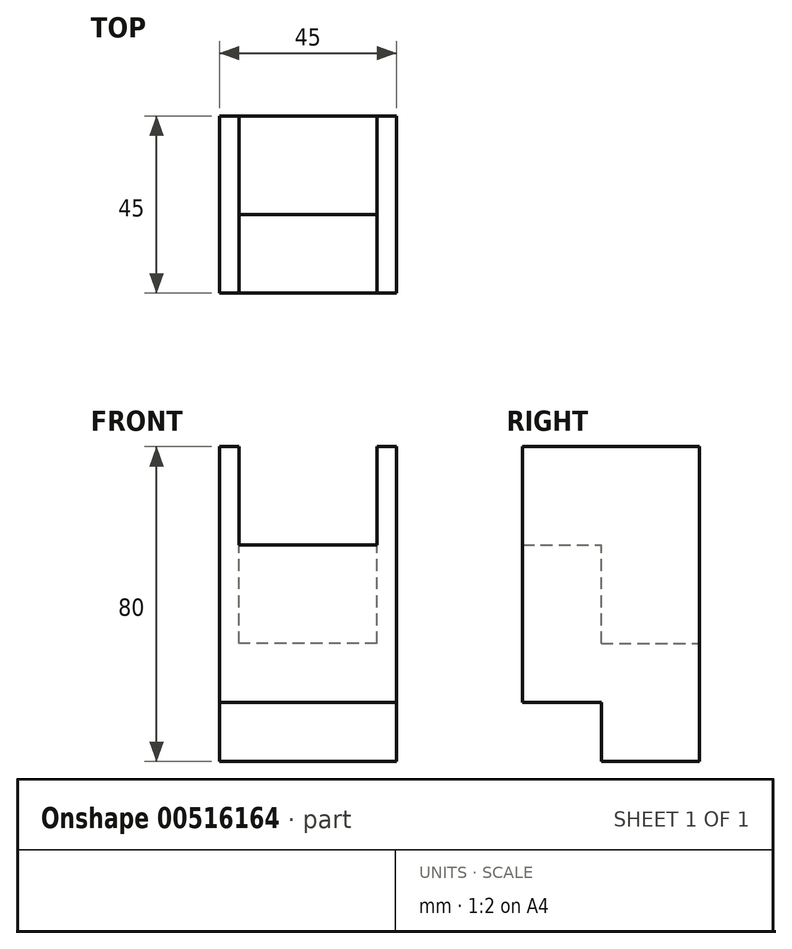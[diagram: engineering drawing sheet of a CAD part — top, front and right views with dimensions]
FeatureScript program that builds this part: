
annotation { "Feature Type Name" : "Feature", "Feature Type Description" : "" }
export const myFeature = defineFeature(function(context is Context, id is Id, definition is map)
    precondition{}
    {
        {
            var Q0;
            Q0=qCreatedBy(makeId("Top.planeOp"),FACE);
            var sketch = newSketch(context, id + "F0", { "sketchPlane" : qUnion([Q0])});
            skLineSegment(sketch, "E0.bottom", {"start": v(22.5, 22.5) * mm, "end": v(-22.5, 22.5) * mm});
            skLineSegment(sketch, "E0.top", {"start": v(22.5, -22.5) * mm, "end": v(-22.5, -22.5) * mm});
            skLineSegment(sketch, "E0.left", {"start": v(22.5, 22.5) * mm, "end": v(22.5, -22.5) * mm});
            skLineSegment(sketch, "E0.right", {"start": v(-22.5, 22.5) * mm, "end": v(-22.5, -22.5) * mm});
            skPoint(sketch, "E0.middle", {"position": v(0, 0) * mm});
            skSolve(sketch);
        }
        {
            var Q0;
            Q0=makeQuery(id+"F0.imprint","IMPRINT",FACE,{"disambiguationData":[TD([[makeQuery(id+"F0.imprint","IMPRINT",EDGE,{"derivedFrom":sQuery(id+"F0.wireOp",EDGE,"E0.bottom")}),1.0]])]});
            extrude(context, id + "F1", {"entities" : qUnion([Q0]), "depth" : 80 * mm, "offsetDistance" : 25 * mm});
        }
        {
            var Q0;
            Q0=makeQuery(id+"F1.opExtrude","CAP_FACE",FACE,{"disambiguationData":[OSD([sQuery(id+"F0.wireOp",EDGE,"E0.bottom"),sQuery(id+"F0.wireOp",EDGE,"E0.top"),sQuery(id+"F0.wireOp",EDGE,"E0.left"),sQuery(id+"F0.wireOp",EDGE,"E0.right")])],"isStart":false});
            var sketch = newSketch(context, id + "F2", { "sketchPlane" : qUnion([Q0])});
            skLineSegment(sketch, "E1", {"start": v(22.5, -22.5) * mm, "end": v(17.5, -22.5) * mm});
            skLineSegment(sketch, "E2", {"start": v(-22.5, -22.5) * mm, "end": v(-17.5, -22.5) * mm});
            skLineSegment(sketch, "E3", {"start": v(22.5, -22.5) * mm, "end": v(22.5, -2.5) * mm});
            skLineSegment(sketch, "E4", {"start": v(-22.5, -22.5) * mm, "end": v(-22.5, -2.5) * mm});
            skLineSegment(sketch, "E5", {"start": v(-17.5, -22.5) * mm, "end": v(-17.5, 22.5) * mm});
            skLineSegment(sketch, "E6", {"start": v(17.5, -22.5) * mm, "end": v(17.5, 22.5) * mm});
            skLineSegment(sketch, "E7", {"start": v(-22.5, -2.5) * mm, "end": v(22.5, -2.5) * mm});
            skSolve(sketch);
        }
        {
            var Q0;
            Q0=makeQuery(id+"F1.opExtrude","SWEPT_FACE",FACE,{"disambiguationData":[OSD([sQuery(id+"F0.wireOp",EDGE,"E0.top")])]});
            var sketch = newSketch(context, id + "F3", { "sketchPlane" : qUnion([Q0])});
            skLineSegment(sketch, "E8", {"start": v(-22.5, 80) * mm, "end": v(-22.5, 30) * mm});
            skLineSegment(sketch, "E9", {"start": v(22.5, 80) * mm, "end": v(22.5, 55) * mm});
            skLineSegment(sketch, "E10", {"start": v(-22.5, 30) * mm, "end": v(22.5, 30) * mm});
            skLineSegment(sketch, "E11", {"start": v(22.5, 55) * mm, "end": v(-22.5, 55) * mm});
            skLineSegment(sketch, "E12", {"start": v(-22.5, 80) * mm, "end": v(-17.5, 80) * mm});
            skLineSegment(sketch, "E13", {"start": v(22.5, 80) * mm, "end": v(17.5, 80) * mm});
            skLineSegment(sketch, "E14", {"start": v(22.5, 80) * mm, "end": v(22.5, 15) * mm});
            skLineSegment(sketch, "E15", {"start": v(22.5, 15) * mm, "end": v(-22.5, 15) * mm});
            skLineSegment(sketch, "E16", {"start": v(-17.5, 80) * mm, "end": v(-17.5, 30) * mm});
            skLineSegment(sketch, "E17", {"start": v(17.5, 80) * mm, "end": v(17.5, 30) * mm});
            skLineSegment(sketch, "E18", {"start": v(22.5, 80) * mm, "end": v(22.5, 0) * mm});
            skSolve(sketch);
        }
        {
            var Q0;
            {var subQ0=sQuery(id+"F2.wireOp",EDGE,"E5");var subQ3=sQuery(id+"F2.wireOp",EDGE,"E7");var subQ4=makeQuery(id+"F2.imprint","INTERSECT",VERTEX,{"derivedFrom":[subQ0,subQ3]});Q0=makeQuery(id+"F2.imprint","IMPRINT",FACE,{"disambiguationData":[TD([[makeQuery(id+"F2.imprint","IMPRINT",EDGE,{"disambiguationData":[TD([[subQ4,-1.0]])],"derivedFrom":subQ3}),-1.0]])]});}
            extrude(context, id + "F4", {"entities" : qUnion([Q0]), "operationType" : NewBodyOperationType.REMOVE, "oppositeDirection" : true, "depth" : 25 * mm, "offsetDistance" : 25 * mm});
        }
        {
            var Q0;
            {var subQ0=sQuery(id+"F2.wireOp",EDGE,"E5");var subQ1=makeQuery(id+"F1.opExtrude","CAP_EDGE",EDGE,{"disambiguationData":[OSD([sQuery(id+"F0.wireOp",EDGE,"E0.bottom")])],"isStart":false});var subQ2=makeQuery(id+"F2.imprint","INTERSECT",VERTEX,{"derivedFrom":[subQ1,subQ0]});Q0=makeQuery(id+"F2.imprint","IMPRINT",FACE,{"disambiguationData":[TD([[makeQuery(id+"F2.imprint","IMPRINT",EDGE,{"disambiguationData":[TD([[subQ2,1.0]])],"derivedFrom":subQ0}),-1.0]])]});}
            extrude(context, id + "F5", {"entities" : qUnion([Q0]), "operationType" : NewBodyOperationType.REMOVE, "oppositeDirection" : true, "depth" : 50 * mm, "offsetDistance" : 25 * mm});
        }
        {
            var Q0;
            {var subQ0=sQuery(id+"F3.wireOp",EDGE,"E15");Q0=makeQuery(id+"F3.imprint","IMPRINT",FACE,{"disambiguationData":[TD([[makeQuery(id+"F3.imprint","IMPRINT",EDGE,{"derivedFrom":subQ0}),1.0]])]});}
            extrude(context, id + "F6", {"entities" : qUnion([Q0]), "operationType" : NewBodyOperationType.REMOVE, "oppositeDirection" : true, "depth" : 20 * mm, "offsetDistance" : 25 * mm});
        }
    });
